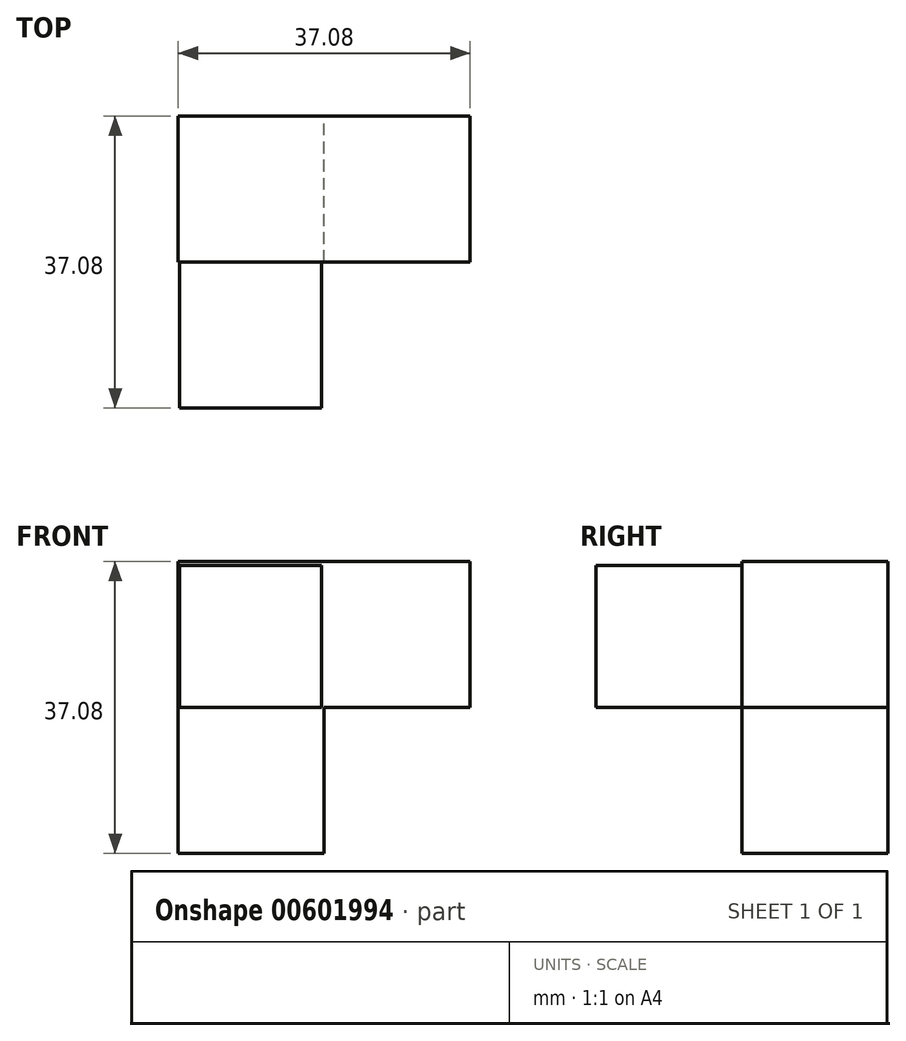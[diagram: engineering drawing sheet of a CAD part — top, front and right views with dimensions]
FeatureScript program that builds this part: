
annotation { "Feature Type Name" : "Feature", "Feature Type Description" : "" }
export const myFeature = defineFeature(function(context is Context, id is Id, definition is map)
    precondition{}
    {
        {
            var Q0;
            Q0=qCreatedBy(makeId("Front.planeOp"),FACE);
            var sketch = newSketch(context, id + "F0", { "sketchPlane" : qUnion([Q0])});
            skLineSegment(sketch, "E0", {"start": v(-20.7, 18.54) * mm, "end": v(-20.7, -18.54) * mm});
            skLineSegment(sketch, "E1", {"start": v(-20.7, -18.54) * mm, "end": v(-2.17, -18.54) * mm});
            skLineSegment(sketch, "E2", {"start": v(-2.17, -18.54) * mm, "end": v(-2.17, 0) * mm});
            skLineSegment(sketch, "E3", {"start": v(-2.17, 0) * mm, "end": v(16.37, 0) * mm});
            skLineSegment(sketch, "E4", {"start": v(16.37, 0) * mm, "end": v(16.37, 18.54) * mm});
            skLineSegment(sketch, "E5", {"start": v(16.37, 18.54) * mm, "end": v(-20.7, 18.54) * mm});
            skSolve(sketch);
        }
        {
            var Q0;
            Q0=makeQuery(id+"F0.imprint","IMPRINT",FACE,{"disambiguationData":[TD([[makeQuery(id+"F0.imprint","IMPRINT",EDGE,{"derivedFrom":sQuery(id+"F0.wireOp",EDGE,"E0")}),1.0]])]});
            extrude(context, id + "F1", {"entities" : qUnion([Q0]), "depth" : 18.54 * mm, "offsetDistance" : 25 * mm});
        }
        {
            var Q0;
            Q0=qCreatedBy(makeId("Front.planeOp"),FACE);
            var sketch = newSketch(context, id + "F2", { "sketchPlane" : qUnion([Q0])});
            skLineSegment(sketch, "E6.bottom", {"start": v(-20.57, 18.05) * mm, "end": v(-2.52, 18.05) * mm});
            skLineSegment(sketch, "E6.top", {"start": v(-20.57, 0) * mm, "end": v(-2.52, 0) * mm});
            skLineSegment(sketch, "E6.left", {"start": v(-20.57, 18.05) * mm, "end": v(-20.57, 0) * mm});
            skLineSegment(sketch, "E6.right", {"start": v(-2.52, 18.05) * mm, "end": v(-2.52, 0) * mm});
            skSolve(sketch);
        }
        {
            var Q0;
            Q0=makeQuery(id+"F2.imprint","IMPRINT",FACE,{"disambiguationData":[TD([[makeQuery(id+"F2.imprint","IMPRINT",EDGE,{"derivedFrom":sQuery(id+"F2.wireOp",EDGE,"E6.bottom")}),-1.0]])]});
            extrude(context, id + "F3", {"entities" : qUnion([Q0]), "operationType" : NewBodyOperationType.ADD, "depth" : 37.08 * mm, "offsetDistance" : 25 * mm});
        }
    });
